# Revit family: Fire-Products_Sprinkler-Systems_YAMATO-PROTEC_TH84Ⅲ
name_source: partatom
category: スプリンクラ
revit_build: Autodesk Revit 2018 (Build: 20170223_1515(x64)
units: mm (PartAtom-declared; Revit-internal decimal feet)

## family parameters
OmniClass タイトル = Fire Fighting Media
OmniClass 番号 = 23.65.70.17.11.31
パーツ タイプ = 標準
ロード時にボイドで切り取り = いいえ
丸型コネクタ寸法 = 直径を使用
作業面ベース = いいえ
共有 = いいえ
常に垂直 = はい
注釈の向きを維持 = いいえ
部屋計算ポイント = はい

## types (1)
- Fire-Products_Sprinkler-Systems_YAMATO-PROTEC_TH84Ⅲ
    Depth = 72  [stored 0.23622 ft]
    Height = 53  [stored 0.173885 ft]
    IfcExportAs = IfcFireSuppressionTerminalType
    IfcExportType = SPRINKLERDEFLECTOR
    OmniClassCode = 23-29 33 11 11 15
    ProductInformation = https://www.yamatoprotec.co.jp
    URL = https://www.yamatoprotec.co.jp
    Uniclass2015Code = Pr_70_55_97_84
    Uniclass2015Title = Sprinkler heads
    Uniclass2015Version = Systems v1.9
    Width = 72  [stored 0.23622 ft]
    モデル = TH84Ⅲ
    仕様書バージョン = Version1.0
    企業コード = 580077214
    分類コード = 50903001200000
    呼称 = スプリンクラーヘッド
    形式 = 放水型
    有効散水半径 = 2300
    積算_科目 = 9 消火設備
    製品リリース年月 = 平成29年12月13日
    製造元 = ヤマトプロテック株式会社
    規定放水圧力 = 100000.0 Pa
    規定放水量 = 84.0 L/min
    認定番号 = S015H024
    説明 = 放水型スプリンクラーヘッド　TH84Ⅲ
    警戒範囲 = はい
    質量 = 0.20 kg

note: [stored X ft] marks values corroborated as IEEE doubles in the binary element streams (Revit-internal decimal feet)
